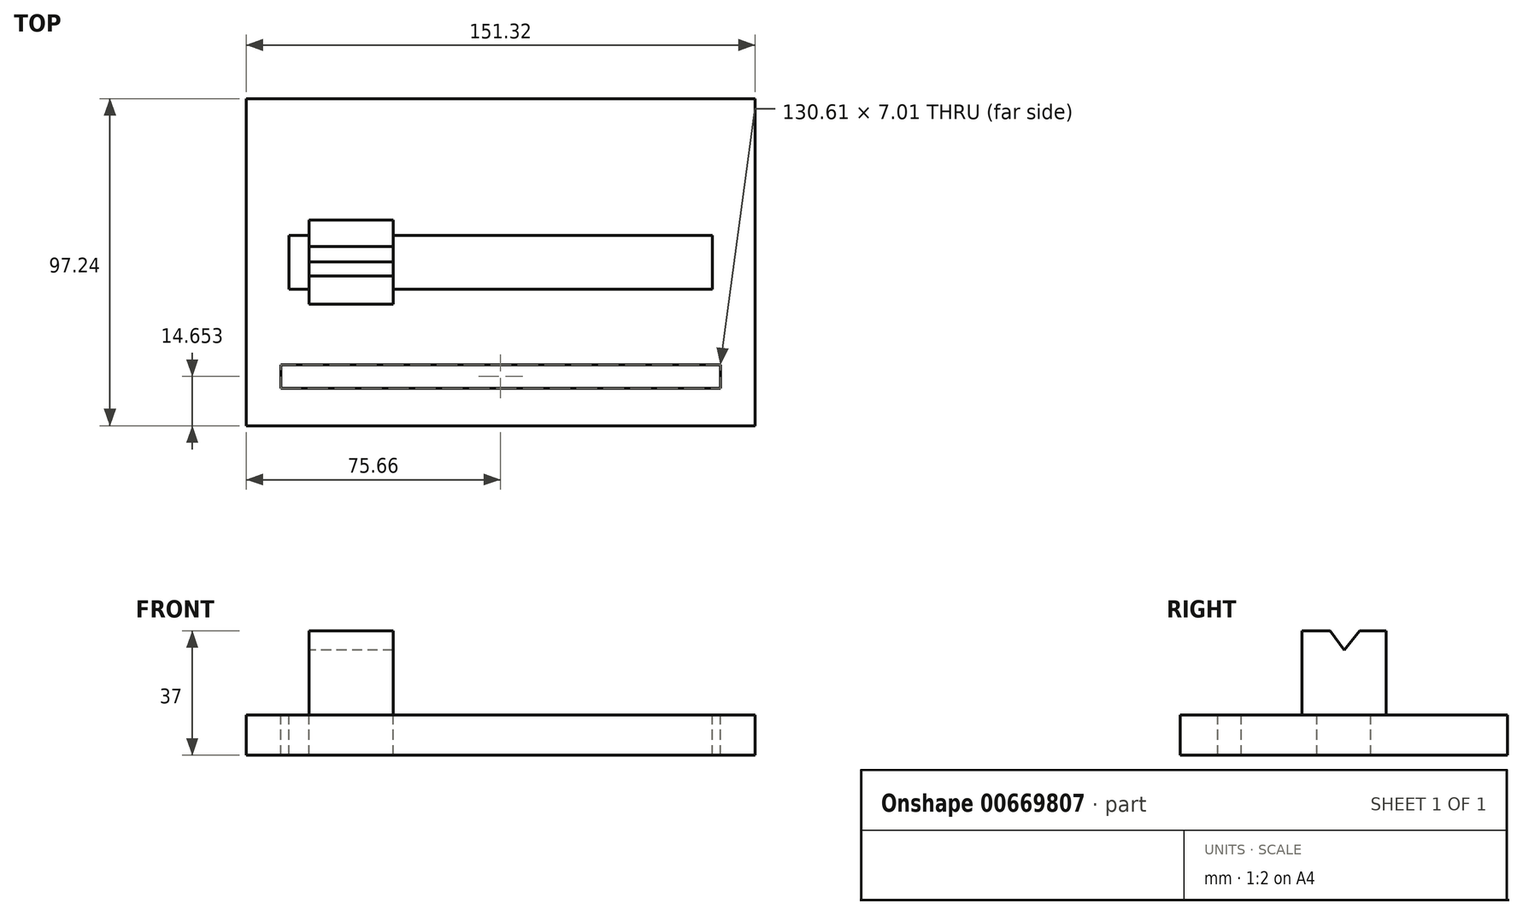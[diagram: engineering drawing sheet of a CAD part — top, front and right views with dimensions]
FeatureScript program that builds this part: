
annotation { "Feature Type Name" : "Feature", "Feature Type Description" : "" }
export const myFeature = defineFeature(function(context is Context, id is Id, definition is map)
    precondition{}
    {
        {
            var Q0;
            Q0=qCreatedBy(makeId("Top.planeOp"),FACE);
            var sketch = newSketch(context, id + "F0", { "sketchPlane" : qUnion([Q0])});
            skLineSegment(sketch, "E0.bottom", {"start": v(-75.66, 48.62) * mm, "end": v(75.66, 48.62) * mm});
            skLineSegment(sketch, "E0.top", {"start": v(-75.66, -48.62) * mm, "end": v(75.66, -48.62) * mm});
            skLineSegment(sketch, "E0.left", {"start": v(-75.66, 48.62) * mm, "end": v(-75.66, -48.62) * mm});
            skLineSegment(sketch, "E0.right", {"start": v(75.66, 48.62) * mm, "end": v(75.66, -48.62) * mm});
            skPoint(sketch, "E0.middle", {"position": v(0, 0) * mm});
            skLineSegment(sketch, "E1.bottom", {"start": v(-62.96, 8) * mm, "end": v(62.96, 8) * mm});
            skLineSegment(sketch, "E1.top", {"start": v(-62.96, -8) * mm, "end": v(62.96, -8) * mm});
            skLineSegment(sketch, "E1.left", {"start": v(-62.96, 8) * mm, "end": v(-62.96, -8) * mm});
            skLineSegment(sketch, "E1.right", {"start": v(62.96, 8) * mm, "end": v(62.96, -8) * mm});
            skLineSegment(sketch, "E2.bottom", {"start": v(-56.96, 12.5) * mm, "end": v(-31.96, 12.5) * mm});
            skLineSegment(sketch, "E2.top", {"start": v(-56.96, -12.5) * mm, "end": v(-31.96, -12.5) * mm});
            skLineSegment(sketch, "E2.left", {"start": v(-56.96, 12.5) * mm, "end": v(-56.96, -12.5) * mm});
            skLineSegment(sketch, "E2.right", {"start": v(-31.96, 12.5) * mm, "end": v(-31.96, -12.5) * mm});
            skPoint(sketch, "E2.middle", {"position": v(-44.46, 0) * mm});
            skLineSegment(sketch, "E3.bottom", {"start": v(-66.25, 12) * mm, "end": v(66.25, 12) * mm});
            skLineSegment(sketch, "E3.top", {"start": v(-66.25, -12) * mm, "end": v(66.25, -12) * mm});
            skLineSegment(sketch, "E3.left", {"start": v(-66.25, 12) * mm, "end": v(-66.25, -12) * mm});
            skLineSegment(sketch, "E3.right", {"start": v(66.25, 12) * mm, "end": v(66.25, -12) * mm});
            skLineSegment(sketch, "E4.bottom", {"start": v(-65.3, -37.47) * mm, "end": v(65.3, -37.47) * mm});
            skLineSegment(sketch, "E4.top", {"start": v(-65.3, -30.46) * mm, "end": v(65.3, -30.46) * mm});
            skLineSegment(sketch, "E4.left", {"start": v(-65.3, -37.47) * mm, "end": v(-65.3, -30.46) * mm});
            skLineSegment(sketch, "E4.right", {"start": v(65.3, -37.47) * mm, "end": v(65.3, -30.46) * mm});
            skPoint(sketch, "E4.middle", {"position": v(0, -33.97) * mm});
            skSolve(sketch);
        }
        {
            var Q0;
            Q0=makeQuery(id+"F0.imprint","IMPRINT",FACE,{"disambiguationData":[TD([[makeQuery(id+"F0.imprint","IMPRINT",EDGE,{"derivedFrom":sQuery(id+"F0.wireOp",EDGE,"E0.bottom")}),-1.0]])]});
            var Q1;
            {var subQ0=sQuery(id+"F0.wireOp",EDGE,"E2.left");var subQ1=sQuery(id+"F0.wireOp",EDGE,"E1.bottom");var subQ2=makeQuery(id+"F0.imprint","INTERSECT",VERTEX,{"derivedFrom":[subQ1,subQ0]});Q1=makeQuery(id+"F0.imprint","IMPRINT",FACE,{"disambiguationData":[TD([[makeQuery(id+"F0.imprint","IMPRINT",EDGE,{"disambiguationData":[TD([[subQ2,-1.0]])],"derivedFrom":subQ1}),1.0]])]});}
            var Q2;
            {var subQ5=sQuery(id+"F0.wireOp",EDGE,"E1.left");Q2=makeQuery(id+"F0.imprint","IMPRINT",FACE,{"disambiguationData":[TD([[makeQuery(id+"F0.imprint","IMPRINT",EDGE,{"derivedFrom":subQ5}),-1.0]])]});}
            var Q3;
            {var subQ0=sQuery(id+"F0.wireOp",EDGE,"E2.bottom");Q3=makeQuery(id+"F0.imprint","IMPRINT",FACE,{"disambiguationData":[TD([[makeQuery(id+"F0.imprint","IMPRINT",EDGE,{"derivedFrom":subQ0}),-1.0]])]});}
            var Q4;
            {var subQ0=sQuery(id+"F0.wireOp",EDGE,"E2.left");var subQ1=sQuery(id+"F0.wireOp",EDGE,"E1.top");var subQ2=makeQuery(id+"F0.imprint","INTERSECT",VERTEX,{"derivedFrom":[subQ1,subQ0]});Q4=makeQuery(id+"F0.imprint","IMPRINT",FACE,{"disambiguationData":[TD([[makeQuery(id+"F0.imprint","IMPRINT",EDGE,{"disambiguationData":[TD([[subQ2,-1.0]])],"derivedFrom":subQ1}),-1.0]])]});}
            var Q5;
            {var subQ0=sQuery(id+"F0.wireOp",EDGE,"E2.top");Q5=makeQuery(id+"F0.imprint","IMPRINT",FACE,{"disambiguationData":[TD([[makeQuery(id+"F0.imprint","IMPRINT",EDGE,{"derivedFrom":subQ0}),1.0]])]});}
            var Q6;
            {var subQ5=sQuery(id+"F0.wireOp",EDGE,"E1.right");Q6=makeQuery(id+"F0.imprint","IMPRINT",FACE,{"disambiguationData":[TD([[makeQuery(id+"F0.imprint","IMPRINT",EDGE,{"derivedFrom":subQ5}),1.0]])]});}
            extrude(context, id + "F1", {"entities" : qUnion([Q0, Q1, Q2, Q3, Q4, Q5, Q6]), "oppositeDirection" : true, "depth" : 12 * mm, "offsetDistance" : 25.4 * mm});
        }
        {
            var Q0;
            {var subQ0=sQuery(id+"F0.wireOp",EDGE,"E2.top");Q0=makeQuery(id+"F0.imprint","IMPRINT",FACE,{"disambiguationData":[TD([[makeQuery(id+"F0.imprint","IMPRINT",EDGE,{"derivedFrom":subQ0}),1.0]])]});}
            var Q1;
            {var subQ0=sQuery(id+"F0.wireOp",EDGE,"E2.left");var subQ1=sQuery(id+"F0.wireOp",EDGE,"E1.top");var subQ2=makeQuery(id+"F0.imprint","INTERSECT",VERTEX,{"derivedFrom":[subQ1,subQ0]});Q1=makeQuery(id+"F0.imprint","IMPRINT",FACE,{"disambiguationData":[TD([[makeQuery(id+"F0.imprint","IMPRINT",EDGE,{"disambiguationData":[TD([[subQ2,-1.0]])],"derivedFrom":subQ1}),-1.0]])]});}
            var Q2;
            {var subQ0=sQuery(id+"F0.wireOp",EDGE,"E2.left");var subQ1=sQuery(id+"F0.wireOp",EDGE,"E1.bottom");var subQ2=makeQuery(id+"F0.imprint","INTERSECT",VERTEX,{"derivedFrom":[subQ1,subQ0]});Q2=makeQuery(id+"F0.imprint","IMPRINT",FACE,{"disambiguationData":[TD([[makeQuery(id+"F0.imprint","IMPRINT",EDGE,{"disambiguationData":[TD([[subQ2,-1.0]])],"derivedFrom":subQ1}),-1.0]])]});}
            var Q3;
            {var subQ0=sQuery(id+"F0.wireOp",EDGE,"E2.left");var subQ1=sQuery(id+"F0.wireOp",EDGE,"E1.bottom");var subQ2=makeQuery(id+"F0.imprint","INTERSECT",VERTEX,{"derivedFrom":[subQ1,subQ0]});Q3=makeQuery(id+"F0.imprint","IMPRINT",FACE,{"disambiguationData":[TD([[makeQuery(id+"F0.imprint","IMPRINT",EDGE,{"disambiguationData":[TD([[subQ2,-1.0]])],"derivedFrom":subQ1}),1.0]])]});}
            var Q4;
            {var subQ0=sQuery(id+"F0.wireOp",EDGE,"E2.bottom");Q4=makeQuery(id+"F0.imprint","IMPRINT",FACE,{"disambiguationData":[TD([[makeQuery(id+"F0.imprint","IMPRINT",EDGE,{"derivedFrom":subQ0}),-1.0]])]});}
            extrude(context, id + "F2", {"entities" : qUnion([Q0, Q1, Q2, Q3, Q4]), "depth" : 25 * mm, "offsetDistance" : 25 * mm});
        }
        {
            var Q0;
            {var subQ0=sQuery(id+"F0.wireOp",EDGE,"E2.left");var subQ1=sQuery(id+"F0.wireOp",EDGE,"E1.bottom");var subQ2=makeQuery(id+"F0.imprint","INTERSECT",VERTEX,{"derivedFrom":[subQ1,subQ0]});Q0=makeQuery(id+"F0.imprint","IMPRINT",FACE,{"disambiguationData":[TD([[makeQuery(id+"F0.imprint","IMPRINT",EDGE,{"disambiguationData":[TD([[subQ2,-1.0]])],"derivedFrom":subQ1}),-1.0]])]});}
            var Q1;
            Q1=makeQuery(id+"F1.opExtrude","CAP_FACE",FACE,{"disambiguationData":[OSD([sQuery(id+"F0.wireOp",EDGE,"E0.bottom"),sQuery(id+"F0.wireOp",EDGE,"E0.top"),sQuery(id+"F0.wireOp",EDGE,"E0.left"),sQuery(id+"F0.wireOp",EDGE,"E0.right"),sQuery(id+"F0.wireOp",EDGE,"E1.bottom"),sQuery(id+"F0.wireOp",EDGE,"E1.top"),sQuery(id+"F0.wireOp",EDGE,"E1.left"),sQuery(id+"F0.wireOp",EDGE,"E1.right")])],"isStart":false});
            extrude(context, id + "F3", {"entities" : qUnion([Q0]), "operationType" : NewBodyOperationType.ADD, "endBound" : BoundingType.UP_TO_SURFACE, "oppositeDirection" : true, "depth" : 25 * mm, "endBoundEntityFace" : qUnion([Q1]), "offsetDistance" : 25 * mm});
        }
        {
            var Q0;
            {var subQ0=sQuery(id+"F0.wireOp",EDGE,"E2.left");Q0=makeQuery(id+"F3.boolean.opBoolean","MERGE",FACE,{"derivedFrom":[makeQuery(id+"F2.opExtrude","SWEPT_FACE",FACE,{"disambiguationData":[OSD([subQ0])]}),makeQuery(id+"F3.opExtrude","SWEPT_FACE",FACE,{"disambiguationData":[OSD([subQ0])]})]});}
            var sketch = newSketch(context, id + "F4", { "sketchPlane" : qUnion([Q0])});
            skLineSegment(sketch, "E5", {"start": v(-4.63, 25) * mm, "end": v(0, 19.17) * mm});
            skLineSegment(sketch, "E6", {"start": v(-0.27, 18.96) * mm, "end": v(4.09, 25) * mm});
            skSolve(sketch);
        }
        {
            var Q0;
            {var subQ0=sQuery(id+"F4.wireOp",EDGE,"E5");var subQ1=makeQuery(id+"F2.opExtrude","CAP_EDGE",EDGE,{"disambiguationData":[OSD([sQuery(id+"F0.wireOp",EDGE,"E2.left")])],"isStart":false});var subQ2=makeQuery(id+"F4.imprint","INTERSECT",VERTEX,{"derivedFrom":[subQ1,subQ0]});Q0=makeQuery(id+"F4.imprint","IMPRINT",FACE,{"disambiguationData":[TD([[makeQuery(id+"F4.imprint","IMPRINT",EDGE,{"disambiguationData":[TD([[subQ2,-1.0]])],"derivedFrom":subQ0}),1.0]])]});}
            extrude(context, id + "F5", {"entities" : qUnion([Q0]), "operationType" : NewBodyOperationType.REMOVE, "oppositeDirection" : true, "depth" : 25 * mm, "offsetDistance" : 25 * mm});
        }
    });
